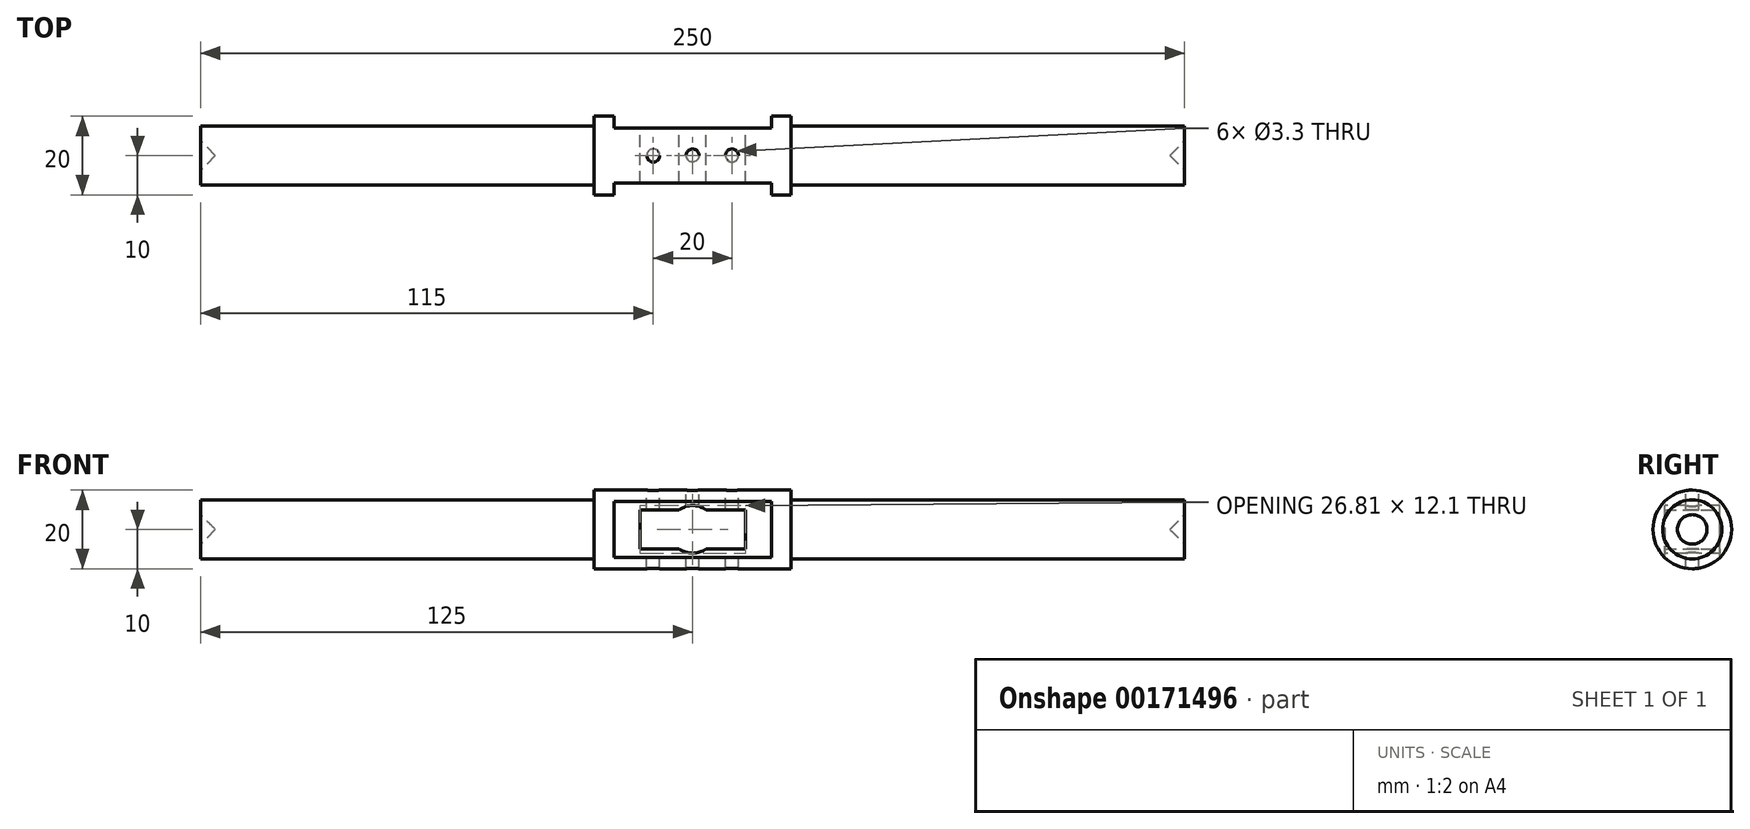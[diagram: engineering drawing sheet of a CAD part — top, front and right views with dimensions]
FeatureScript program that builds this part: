
annotation { "Feature Type Name" : "Feature", "Feature Type Description" : "" }
export const myFeature = defineFeature(function(context is Context, id is Id, definition is map)
    precondition{}
    {
        {
            var Q0;
            Q0=qCreatedBy(makeId("Front.planeOp"),FACE);
            var sketch = newSketch(context, id + "F0", { "sketchPlane" : qUnion([Q0])});
            skLineSegment(sketch, "E0", {"start": v(-160.41, 0) * mm, "end": v(0, 0) * mm, "construction": true});
            skLineSegment(sketch, "E1", {"start": v(-125, 3.75) * mm, "end": v(-125, 7.5) * mm});
            skLineSegment(sketch, "E2", {"start": v(-125, 7.5) * mm, "end": v(-25, 7.5) * mm});
            skLineSegment(sketch, "E3", {"start": v(-25, 7.5) * mm, "end": v(-25, 10) * mm});
            skLineSegment(sketch, "E4", {"start": v(-25, 10) * mm, "end": v(25, 10) * mm});
            skLineSegment(sketch, "E5", {"start": v(25, 10) * mm, "end": v(25, 7.5) * mm});
            skLineSegment(sketch, "E6", {"start": v(25, 7.5) * mm, "end": v(125, 7.5) * mm});
            skLineSegment(sketch, "E7", {"start": v(125, 7.5) * mm, "end": v(125, 3.75) * mm});
            skLineSegment(sketch, "E8", {"start": v(0, 34.12) * mm, "end": v(0, 0) * mm, "construction": true});
            skLineSegment(sketch, "E9", {"start": v(0, 0) * mm, "end": v(130.7, 0) * mm, "construction": true});
            skLineSegment(sketch, "E10", {"start": v(-121.25, 0) * mm, "end": v(121.25, 0) * mm});
            skLineSegment(sketch, "E11", {"start": v(-125, 3.75) * mm, "end": v(-121.25, 0) * mm});
            skPoint(sketch, "E12.orphan", {"position": v(-125, 0) * mm});
            skLineSegment(sketch, "E13", {"start": v(125, 3.75) * mm, "end": v(121.25, 0) * mm});
            skPoint(sketch, "E14.orphan", {"position": v(125, 0) * mm});
            skSolve(sketch);
        }
        {
            var Q0;
            Q0=makeQuery(id+"F0.imprint","IMPRINT",FACE,{"disambiguationData":[TD([[makeQuery(id+"F0.imprint","IMPRINT",EDGE,{"derivedFrom":sQuery(id+"F0.wireOp",EDGE,"E1")}),-1.0]])]});
            var Q1;
            Q1=sQuery(id+"F0.wireOp",EDGE,"E0");
            revolve(context, id + "F1", {"entities" : qUnion([Q0]), "axis" : qUnion([Q1]), "revolveType" : RevolveType.FULL});
        }
        {
            var Q0;
            Q0=qCreatedBy(makeId("Top.planeOp"),FACE);
            cPlane(context, id + "F2", {"entities" : qUnion([Q0]), "cplaneType" : CPlaneType.OFFSET, "offset" : 25 * mm, "width" : 150 * mm, "height" : 150 * mm});
        }
        {
            var Q0;
            Q0=qCreatedBy(id+"F2.planeOp",FACE);
            var sketch = newSketch(context, id + "F3", { "sketchPlane" : qUnion([Q0])});
            skLineSegment(sketch, "E15.bottom", {"start": v(-20, 12) * mm, "end": v(20, 12) * mm});
            skLineSegment(sketch, "E15.top", {"start": v(-20, 7) * mm, "end": v(20, 7) * mm});
            skLineSegment(sketch, "E15.left", {"start": v(-20, 12) * mm, "end": v(-20, 7) * mm});
            skLineSegment(sketch, "E15.right", {"start": v(20, 12) * mm, "end": v(20, 7) * mm});
            skLineSegment(sketch, "E16.bottom", {"start": v(-20, -7) * mm, "end": v(20, -7) * mm});
            skLineSegment(sketch, "E16.top", {"start": v(-20, -12) * mm, "end": v(20, -12) * mm});
            skLineSegment(sketch, "E16.left", {"start": v(-20, -12) * mm, "end": v(-20, -7) * mm});
            skLineSegment(sketch, "E16.right", {"start": v(20, -12) * mm, "end": v(20, -7) * mm});
            skLineSegment(sketch, "E17", {"start": v(-12.94, 0) * mm, "end": v(0, 0) * mm, "construction": true});
            skLineSegment(sketch, "E18", {"start": v(0, 0) * mm, "end": v(0, 10.56) * mm, "construction": true});
            skLineSegment(sketch, "E19", {"start": v(0, 0) * mm, "end": v(11.5, 0) * mm, "construction": true});
            skSolve(sketch);
        }
        {
            var Q0;
            Q0=makeQuery(id+"F3.imprint","IMPRINT",FACE,{"disambiguationData":[TD([[makeQuery(id+"F3.imprint","IMPRINT",EDGE,{"derivedFrom":sQuery(id+"F3.wireOp",EDGE,"E15.bottom")}),-1.0]])]});
            var Q1;
            Q1=makeQuery(id+"F3.imprint","IMPRINT",FACE,{"disambiguationData":[TD([[makeQuery(id+"F3.imprint","IMPRINT",EDGE,{"derivedFrom":sQuery(id+"F3.wireOp",EDGE,"E16.bottom")}),-1.0]])]});
            var Q2;
            Q2=makeQuery(id+"F1.opRevolve","SWEPT_BODY",BODY,{"disambiguationData":[OSD([sQuery(id+"F0.wireOp",EDGE,"E1"),sQuery(id+"F0.wireOp",EDGE,"E2"),sQuery(id+"F0.wireOp",EDGE,"E3"),sQuery(id+"F0.wireOp",EDGE,"E4"),sQuery(id+"F0.wireOp",EDGE,"E5"),sQuery(id+"F0.wireOp",EDGE,"E6"),sQuery(id+"F0.wireOp",EDGE,"E7"),sQuery(id+"F0.wireOp",EDGE,"E10")])]});
            extrude(context, id + "F4", {"entities" : qUnion([Q0, Q1]), "operationType" : NewBodyOperationType.REMOVE, "endBound" : BoundingType.THROUGH_ALL, "oppositeDirection" : true, "endBoundEntityBody" : qUnion([Q2]), "depth" : 25 * mm});
        }
        {
            var Q0;
            Q0=makeQuery(id+"F4.boolean.opBoolean","COPY",FACE,{"derivedFrom":makeQuery(id+"F4.opExtrude","SWEPT_FACE",FACE,{"disambiguationData":[OSD([sQuery(id+"F3.wireOp",EDGE,"E15.top")])]})});
            var sketch = newSketch(context, id + "F5", { "sketchPlane" : qUnion([Q0])});
            skPoint(sketch, "E20", {"position": v(0, 0) * mm});
            skSolve(sketch);
        }
        {
            var Q0;
            Q0=sQuery(id+"F5.wireOp",VERTEX,"E20");
            var Q1;
            Q1=makeQuery(id+"F1.opRevolve","SWEPT_BODY",BODY,{"disambiguationData":[OSD([sQuery(id+"F0.wireOp",EDGE,"E1"),sQuery(id+"F0.wireOp",EDGE,"E2"),sQuery(id+"F0.wireOp",EDGE,"E3"),sQuery(id+"F0.wireOp",EDGE,"E4"),sQuery(id+"F0.wireOp",EDGE,"E5"),sQuery(id+"F0.wireOp",EDGE,"E6"),sQuery(id+"F0.wireOp",EDGE,"E7"),sQuery(id+"F0.wireOp",EDGE,"E10")])]});
            hole(context, id + "F6", {"style" : HoleStyle.SIMPLE, "endStyle" : HoleEndStyle.THROUGH, "standardTappedOrClearance" : lookupTablePath({ "standard" : "ISO", "engagement" : "75%", "pitch" : "2 mm", "size" : "M14", "type" : "Tapped" }), "standardBlindInLast" : lookupTablePath({ "standard" : "ISO", "engagement" : "75%", "pitch" : "2 mm", "size" : "M14", "type" : "Tapped" }), "holeDiameter" : 12.1 * mm, "locations" : qUnion([Q0]), "scope" : qUnion([Q1]), "isTappedThrough" : true, "majorDiameter" : 14 * mm, "showTappedDepth" : true, "startStyle" : HoleStartStyle.SKETCH});
        }
        {
            var Q0;
            Q0=qCreatedBy(makeId("Top.planeOp"),FACE);
            cPlane(context, id + "F7", {"entities" : qUnion([Q0]), "cplaneType" : CPlaneType.OFFSET, "offset" : 10 * mm, "oppositeDirection" : true, "width" : 150 * mm, "height" : 150 * mm});
        }
        {
            var Q0;
            Q0=qCreatedBy(id+"F7.planeOp",FACE);
            var sketch = newSketch(context, id + "F8", { "sketchPlane" : qUnion([Q0])});
            skPoint(sketch, "E21", {"position": v(0, 0) * mm});
            skLineSegment(sketch, "E22", {"start": v(-10, 0) * mm, "end": v(0, 0) * mm, "construction": true});
            skLineSegment(sketch, "E23", {"start": v(0, 0) * mm, "end": v(10, 0) * mm, "construction": true});
            skPoint(sketch, "E24", {"position": v(-10, 0) * mm});
            skPoint(sketch, "E25", {"position": v(10, 0) * mm});
            skSolve(sketch);
        }
        {
            var Q0;
            Q0=sQuery(id+"F8.wireOp",VERTEX,"E21");
            var Q1;
            Q1=sQuery(id+"F8.wireOp",VERTEX,"E24");
            var Q2;
            Q2=sQuery(id+"F8.wireOp",VERTEX,"E25");
            var Q3;
            Q3=makeQuery(id+"F1.opRevolve","SWEPT_BODY",BODY,{"disambiguationData":[OSD([sQuery(id+"F0.wireOp",EDGE,"E1"),sQuery(id+"F0.wireOp",EDGE,"E2"),sQuery(id+"F0.wireOp",EDGE,"E3"),sQuery(id+"F0.wireOp",EDGE,"E4"),sQuery(id+"F0.wireOp",EDGE,"E5"),sQuery(id+"F0.wireOp",EDGE,"E6"),sQuery(id+"F0.wireOp",EDGE,"E7"),sQuery(id+"F0.wireOp",EDGE,"E10")])]});
            hole(context, id + "F9", {"style" : HoleStyle.SIMPLE, "endStyle" : HoleEndStyle.THROUGH, "oppositeDirection" : true, "standardTappedOrClearance" : lookupTablePath({ "standard" : "ISO", "fit" : "Normal", "size" : "M3", "type" : "Clearance" }), "standardBlindInLast" : lookupTablePath({ "fit" : "Standard", "standard" : "ISO", "size" : "M3", "type" : "Clearance" }), "holeDiameter" : 3.3 * mm, "locations" : qUnion([Q0, Q1, Q2]), "scope" : qUnion([Q3]), "isTappedThrough" : true, "startStyle" : HoleStartStyle.SKETCH});
        }
        {
            var Q0;
            Q0=makeQuery(id+"F4.boolean.opBoolean","COPY",FACE,{"derivedFrom":makeQuery(id+"F4.opExtrude","SWEPT_FACE",FACE,{"disambiguationData":[OSD([sQuery(id+"F3.wireOp",EDGE,"E15.top")])]})});
            var sketch = newSketch(context, id + "F10", { "sketchPlane" : qUnion([Q0])});
            skLineSegment(sketch, "E26", {"start": v(17.18, 0) * mm, "end": v(0, 0) * mm, "construction": true});
            skLineSegment(sketch, "E27", {"start": v(0, 0) * mm, "end": v(0, -19.77) * mm, "construction": true});
            skPoint(sketch, "E27.endSnap0", {"position": v(0, -7.14) * mm});
            skLineSegment(sketch, "E28.bottom", {"start": v(13.4, -5) * mm, "end": v(3.4, -5) * mm});
            skLineSegment(sketch, "E28.top", {"start": v(13.4, 5) * mm, "end": v(3.4, 5) * mm});
            skLineSegment(sketch, "E28.left", {"start": v(13.4, -5) * mm, "end": v(13.4, 5) * mm});
            skLineSegment(sketch, "E28.right", {"start": v(-13.4, -5) * mm, "end": v(-13.4, 5) * mm});
            skArc(sketch, "E29", {"start": v(-3.4, 5) * mm, "mid": v(-6.05, 0) * mm, "end": v(-3.4, -5) * mm});
            skLineSegment(sketch, "E30.trimOffspring", {"start": v(-3.4, -5) * mm, "end": v(-13.4, -5) * mm});
            skLineSegment(sketch, "E31.trimOffspring", {"start": v(-3.4, 5) * mm, "end": v(-13.4, 5) * mm});
            skArc(sketch, "E32.trimOffspring", {"start": v(3.4, -5) * mm, "mid": v(6.05, 0) * mm, "end": v(3.4, 5) * mm});
            skSolve(sketch);
        }
        {
            var Q0;
            Q0 = qSketchRegion(id + "F10", true);
            extrude(context, id + "F11", {"entities" : qUnion([Q0]), "operationType" : NewBodyOperationType.REMOVE, "endBound" : BoundingType.THROUGH_ALL, "oppositeDirection" : true, "depth" : 25 * mm});
        }
    });
